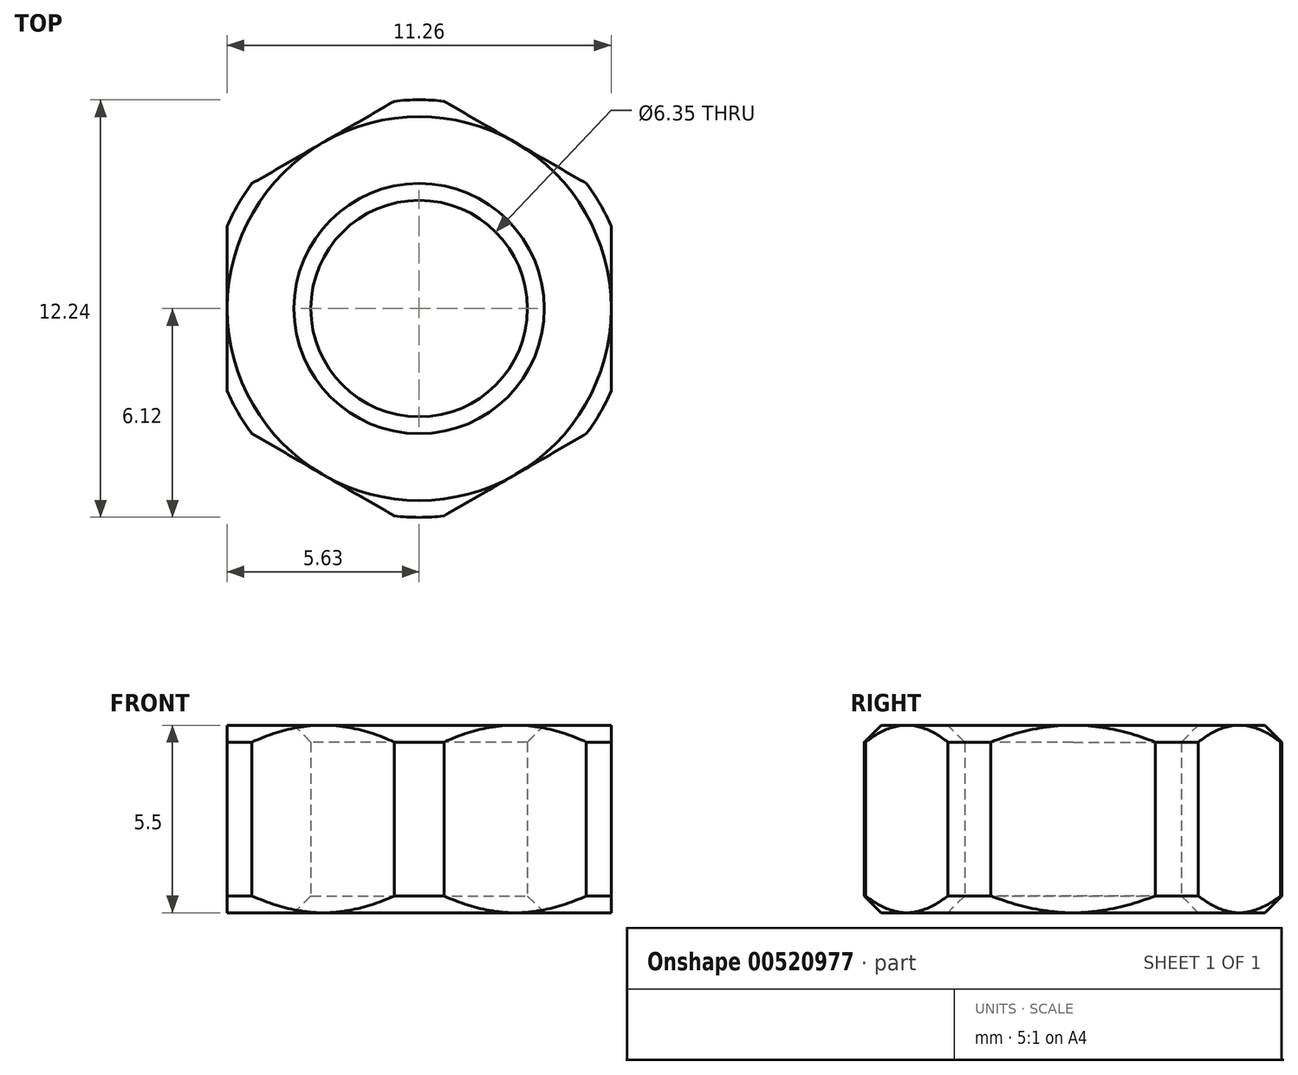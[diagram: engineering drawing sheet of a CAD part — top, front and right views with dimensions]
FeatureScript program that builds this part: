
annotation { "Feature Type Name" : "Feature", "Feature Type Description" : "" }
export const myFeature = defineFeature(function(context is Context, id is Id, definition is map)
    precondition{}
    {
        {
            var Q0;
            Q0=qCreatedBy(makeId("Top.planeOp"),FACE);
            var sketch = newSketch(context, id + "F0", { "sketchPlane" : qUnion([Q0])});
            skLineSegment(sketch, "E0", {"start": v(0, 60) * mm, "end": v(0, -60) * mm});
            skLineSegment(sketch, "E1", {"start": v(-70, 0) * mm, "end": v(70, 0) * mm});
            skCircle(sketch, "E2", {"center": v(0, 0) * mm, "radius": 3.17 * mm});
            skLineSegment(sketch, "E3", {"start": v(0, 6.5) * mm, "end": v(5.63, 3.25) * mm});
            skLineSegment(sketch, "E4", {"start": v(5.63, 3.25) * mm, "end": v(5.63, -3.25) * mm});
            skLineSegment(sketch, "E5", {"start": v(5.63, -3.25) * mm, "end": v(0, -6.5) * mm});
            skLineSegment(sketch, "E6", {"start": v(0, 6.5) * mm, "end": v(-5.63, 3.25) * mm});
            skLineSegment(sketch, "E7", {"start": v(-5.63, 3.25) * mm, "end": v(-5.63, -3.25) * mm});
            skLineSegment(sketch, "E8", {"start": v(-5.63, -3.25) * mm, "end": v(0, -6.5) * mm});
            skSolve(sketch);
        }
        {
            var Q0;
            {var subQ0=sQuery(id+"F0.wireOp",EDGE,"E6");Q0=makeQuery(id+"F0.imprint","IMPRINT",FACE,{"disambiguationData":[TD([[makeQuery(id+"F0.imprint","IMPRINT",EDGE,{"derivedFrom":subQ0}),1.0]])]});}
            var Q1;
            {var subQ5=sQuery(id+"F0.wireOp",EDGE,"E3");Q1=makeQuery(id+"F0.imprint","IMPRINT",FACE,{"disambiguationData":[TD([[makeQuery(id+"F0.imprint","IMPRINT",EDGE,{"derivedFrom":subQ5}),-1.0]])]});}
            var Q2;
            {var subQ7=sQuery(id+"F0.wireOp",EDGE,"E8");Q2=makeQuery(id+"F0.imprint","IMPRINT",FACE,{"disambiguationData":[TD([[makeQuery(id+"F0.imprint","IMPRINT",EDGE,{"derivedFrom":subQ7}),1.0]])]});}
            var Q3;
            {var subQ0=sQuery(id+"F0.wireOp",EDGE,"E5");Q3=makeQuery(id+"F0.imprint","IMPRINT",FACE,{"disambiguationData":[TD([[makeQuery(id+"F0.imprint","IMPRINT",EDGE,{"derivedFrom":subQ0}),-1.0]])]});}
            extrude(context, id + "F1", {"entities" : qUnion([Q0, Q1, Q2, Q3]), "depth" : 5.5 * mm, "offsetDistance" : 25 * mm});
        }
        {
            var Q0;
            Q0=qCreatedBy(makeId("Front.planeOp"),FACE);
            var sketch = newSketch(context, id + "F2", { "sketchPlane" : qUnion([Q0])});
            skLineSegment(sketch, "E9", {"start": v(0, 60) * mm, "end": v(0, -60) * mm});
            skLineSegment(sketch, "E10", {"start": v(-70, 0) * mm, "end": v(70, 0) * mm});
            skLineSegment(sketch, "E11", {"start": v(6.12, 5) * mm, "end": v(6.12, 0.5) * mm});
            skLineSegment(sketch, "E12", {"start": v(3.17, 0.5) * mm, "end": v(3.17, 5) * mm});
            skLineSegment(sketch, "E13", {"start": v(3.67, 5.5) * mm, "end": v(5.63, 5.5) * mm});
            skLineSegment(sketch, "E14", {"start": v(3.67, 0) * mm, "end": v(5.63, 0) * mm});
            skLineSegment(sketch, "E15", {"start": v(3.17, 5) * mm, "end": v(3.67, 5.5) * mm});
            skLineSegment(sketch, "E16", {"start": v(3.17, 0.5) * mm, "end": v(3.67, 0) * mm});
            skLineSegment(sketch, "E17", {"start": v(6.12, 0.5) * mm, "end": v(5.63, 0) * mm});
            skLineSegment(sketch, "E18", {"start": v(6.12, 5) * mm, "end": v(5.63, 5.5) * mm});
            skSolve(sketch);
        }
        {
            var Q0;
            Q0=makeQuery(id+"F2.imprint","IMPRINT",FACE,{"disambiguationData":[TD([[makeQuery(id+"F2.imprint","IMPRINT",EDGE,{"derivedFrom":sQuery(id+"F2.wireOp",EDGE,"E11")}),-1.0]])]});
            var Q1;
            Q1=sQuery(id+"F2.wireOp",EDGE,"E9");
            revolve(context, id + "F3", {"entities" : qUnion([Q0]), "axis" : qUnion([Q1]), "revolveType" : RevolveType.FULL});
        }
        {
            var Q0;
            Q0=makeQuery(id+"F1.opExtrude","SWEPT_BODY",BODY,{"disambiguationData":[OSD([sQuery(id+"F0.wireOp",EDGE,"E2"),sQuery(id+"F0.wireOp",EDGE,"E3"),sQuery(id+"F0.wireOp",EDGE,"E4"),sQuery(id+"F0.wireOp",EDGE,"E5"),sQuery(id+"F0.wireOp",EDGE,"E6"),sQuery(id+"F0.wireOp",EDGE,"E7"),sQuery(id+"F0.wireOp",EDGE,"E8")])]});
            var Q1;
            Q1=makeQuery(id+"F3.opRevolve","SWEPT_BODY",BODY,{"disambiguationData":[OSD([sQuery(id+"F2.wireOp",EDGE,"E11"),sQuery(id+"F2.wireOp",EDGE,"E12"),sQuery(id+"F2.wireOp",EDGE,"E13"),sQuery(id+"F2.wireOp",EDGE,"E14"),sQuery(id+"F2.wireOp",EDGE,"E15"),sQuery(id+"F2.wireOp",EDGE,"E16"),sQuery(id+"F2.wireOp",EDGE,"E17"),sQuery(id+"F2.wireOp",EDGE,"E18")])]});
            booleanBodies(context, id + "F4", {"operationType" : BooleanOperationType.INTERSECTION, "tools" : qUnion([Q0, Q1])});
        }
    });
